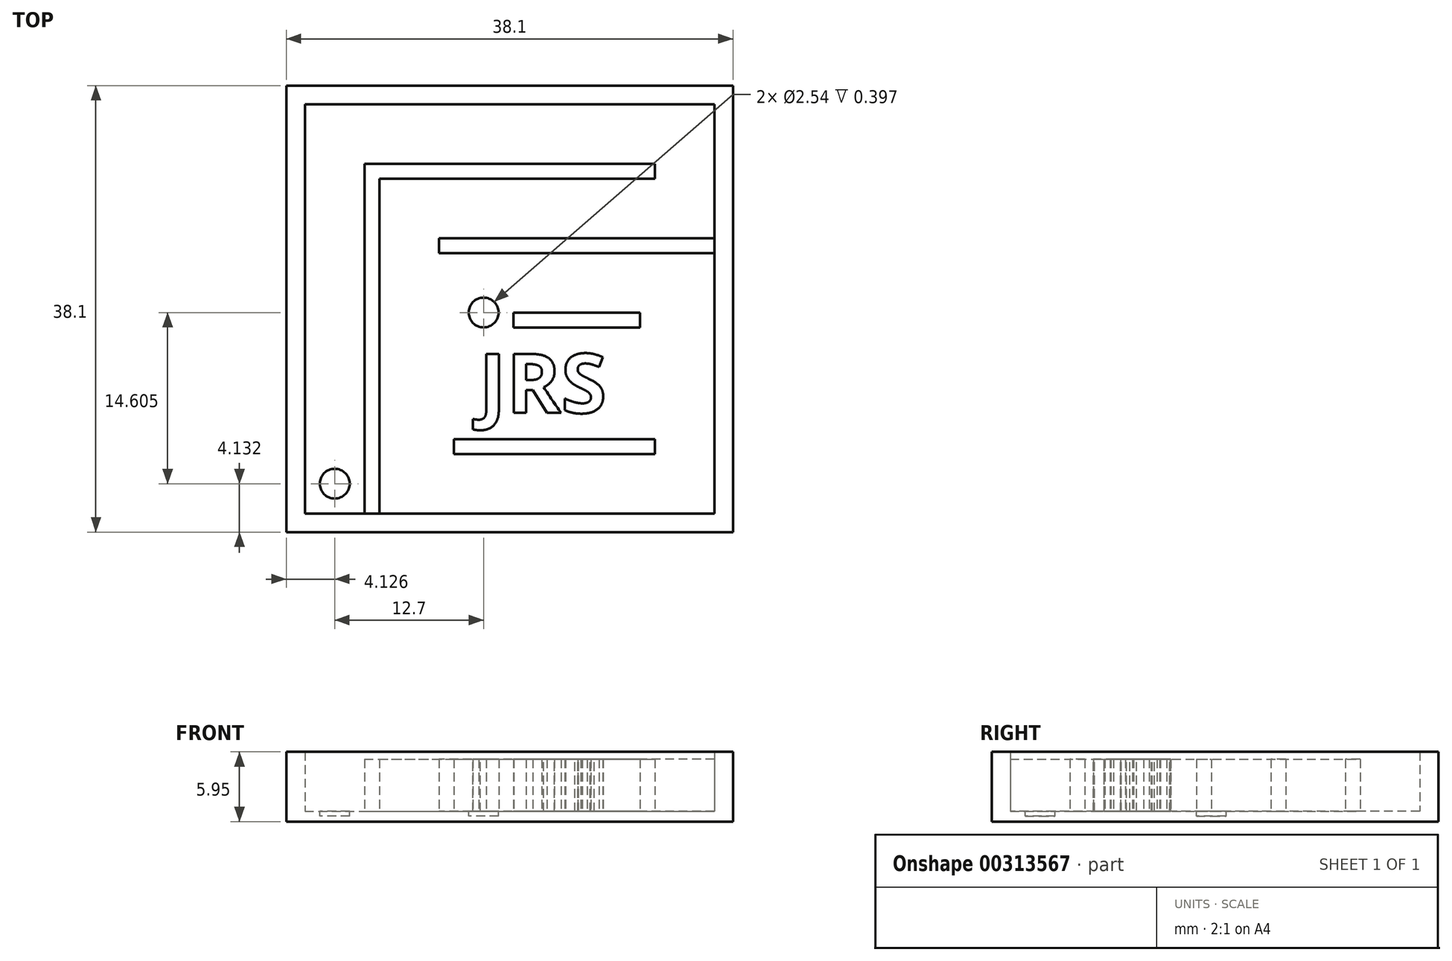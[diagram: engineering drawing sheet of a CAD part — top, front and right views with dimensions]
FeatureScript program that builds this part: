
annotation { "Feature Type Name" : "Feature", "Feature Type Description" : "" }
export const myFeature = defineFeature(function(context is Context, id is Id, definition is map)
    precondition{}
    {
        {
            var Q0;
            Q0=qCreatedBy(makeId("Top.planeOp"),FACE);
            var sketch = newSketch(context, id + "F0", { "sketchPlane" : qUnion([Q0])});
            skLineSegment(sketch, "E0.bottom", {"start": v(-20.77, 18.13) * mm, "end": v(17.33, 18.13) * mm});
            skLineSegment(sketch, "E0.top", {"start": v(-20.77, -19.97) * mm, "end": v(17.33, -19.97) * mm});
            skLineSegment(sketch, "E0.left", {"start": v(-20.77, 18.13) * mm, "end": v(-20.77, -19.97) * mm});
            skLineSegment(sketch, "E0.right", {"start": v(17.33, 18.13) * mm, "end": v(17.33, -19.97) * mm});
            skSolve(sketch);
        }
        {
            var Q0;
            Q0=makeQuery(id+"F0.imprint","IMPRINT",FACE,{"disambiguationData":[TD([[makeQuery(id+"F0.imprint","IMPRINT",EDGE,{"derivedFrom":sQuery(id+"F0.wireOp",EDGE,"E0.bottom")}),-1.0]])]});
            extrude(context, id + "F1", {"entities" : qUnion([Q0]), "depth" : 0.08 * mm});
        }
        {
            var Q0;
            Q0=makeQuery(id+"F1.opExtrude","CAP_FACE",FACE,{"disambiguationData":[OSD([sQuery(id+"F0.wireOp",EDGE,"E0.bottom"),sQuery(id+"F0.wireOp",EDGE,"E0.top"),sQuery(id+"F0.wireOp",EDGE,"E0.left"),sQuery(id+"F0.wireOp",EDGE,"E0.right")])],"isStart":false});
            var sketch = newSketch(context, id + "F2", { "sketchPlane" : qUnion([Q0])});
            skLineSegment(sketch, "E1.0", {"start": v(-19.18, 16.55) * mm, "end": v(15.74, 16.55) * mm});
            skLineSegment(sketch, "E1.1", {"start": v(-19.18, 16.55) * mm, "end": v(-19.18, -18.38) * mm});
            skLineSegment(sketch, "E1.2", {"start": v(-19.18, -18.38) * mm, "end": v(15.74, -18.38) * mm});
            skLineSegment(sketch, "E1.3", {"start": v(15.74, 16.55) * mm, "end": v(15.74, -18.38) * mm});
            skSolve(sketch);
        }
        {
            var Q0;
            Q0=makeQuery(id+"F2.imprint","IMPRINT",FACE,{"disambiguationData":[TD([[makeQuery(id+"F2.imprint","IMPRINT",EDGE,{"derivedFrom":sQuery(id+"F2.wireOp",EDGE,"E1.0")}),1.0]])]});
            extrude(context, id + "F3", {"entities" : qUnion([Q0]), "operationType" : NewBodyOperationType.ADD, "depth" : 5.08 * mm});
        }
        {
            var Q0;
            Q0=makeQuery(id+"F1.opExtrude","CAP_FACE",FACE,{"disambiguationData":[OSD([sQuery(id+"F0.wireOp",EDGE,"E0.bottom"),sQuery(id+"F0.wireOp",EDGE,"E0.top"),sQuery(id+"F0.wireOp",EDGE,"E0.left"),sQuery(id+"F0.wireOp",EDGE,"E0.right")])],"isStart":false});
            var sketch = newSketch(context, id + "F4", { "sketchPlane" : qUnion([Q0])});
            skLineSegment(sketch, "E2.bottom", {"start": v(-14.1, -18.38) * mm, "end": v(-12.83, -18.38) * mm});
            skLineSegment(sketch, "E2.top", {"start": v(-14.1, 11.47) * mm, "end": v(-12.83, 11.47) * mm});
            skLineSegment(sketch, "E2.left", {"start": v(-14.1, -18.38) * mm, "end": v(-14.1, 11.47) * mm});
            skLineSegment(sketch, "E2.right", {"start": v(-12.83, -18.38) * mm, "end": v(-12.83, 11.47) * mm});
            skLineSegment(sketch, "E3.bottom", {"start": v(-12.83, 11.47) * mm, "end": v(10.66, 11.47) * mm});
            skLineSegment(sketch, "E3.top", {"start": v(-12.83, 10.2) * mm, "end": v(10.66, 10.2) * mm});
            skLineSegment(sketch, "E3.left", {"start": v(-12.83, 11.47) * mm, "end": v(-12.83, 10.2) * mm});
            skLineSegment(sketch, "E3.right", {"start": v(10.66, 11.47) * mm, "end": v(10.66, 10.2) * mm});
            skLineSegment(sketch, "E4.bottom", {"start": v(15.74, 3.85) * mm, "end": v(-7.75, 3.85) * mm});
            skLineSegment(sketch, "E4.top", {"start": v(15.74, 5.12) * mm, "end": v(-7.75, 5.12) * mm});
            skLineSegment(sketch, "E4.left", {"start": v(15.74, 3.85) * mm, "end": v(15.74, 5.12) * mm});
            skLineSegment(sketch, "E4.right", {"start": v(-7.75, 3.85) * mm, "end": v(-7.75, 5.12) * mm});
            skLineSegment(sketch, "E5.bottom", {"start": v(-7.75, 3.85) * mm, "end": v(-6.48, 3.85) * mm});
            skLineSegment(sketch, "E5.top", {"start": v(-7.75, -13.3) * mm, "end": v(-6.48, -13.3) * mm});
            skLineSegment(sketch, "E5.left", {"start": v(-7.75, 3.85) * mm, "end": v(-7.75, -13.3) * mm});
            skLineSegment(sketch, "E5.right", {"start": v(-6.48, 3.85) * mm, "end": v(-6.48, -13.3) * mm});
            skLineSegment(sketch, "E6.bottom", {"start": v(-6.48, -13.3) * mm, "end": v(10.66, -13.3) * mm});
            skLineSegment(sketch, "E6.top", {"start": v(-6.48, -12.04) * mm, "end": v(10.66, -12.04) * mm});
            skLineSegment(sketch, "E6.left", {"start": v(-6.48, -13.3) * mm, "end": v(-6.48, -12.04) * mm});
            skLineSegment(sketch, "E6.right", {"start": v(10.66, -13.3) * mm, "end": v(10.66, -12.04) * mm});
            skLineSegment(sketch, "E7.bottom", {"start": v(10.66, -12.04) * mm, "end": v(9.4, -12.04) * mm});
            skLineSegment(sketch, "E7.top", {"start": v(10.66, -1.23) * mm, "end": v(9.4, -1.23) * mm});
            skLineSegment(sketch, "E7.left", {"start": v(10.66, -12.04) * mm, "end": v(10.66, -1.23) * mm});
            skLineSegment(sketch, "E7.right", {"start": v(9.4, -12.04) * mm, "end": v(9.4, -1.23) * mm});
            skLineSegment(sketch, "E8.bottom", {"start": v(9.4, -1.23) * mm, "end": v(-1.4, -1.23) * mm});
            skLineSegment(sketch, "E8.top", {"start": v(9.4, -2.5) * mm, "end": v(-1.4, -2.5) * mm});
            skLineSegment(sketch, "E8.left", {"start": v(9.4, -1.23) * mm, "end": v(9.4, -2.5) * mm});
            skLineSegment(sketch, "E8.right", {"start": v(-1.4, -1.23) * mm, "end": v(-1.4, -2.5) * mm});
            skCircle(sketch, "E9", {"center": v(-3.94, -1.23) * mm, "radius": 1.27 * mm});
            skCircle(sketch, "E10", {"center": v(-16.64, -15.84) * mm, "radius": 1.27 * mm});
            skSolve(sketch);
        }
        {
            var Q0;
            Q0=makeQuery(id+"F4.imprint","IMPRINT",FACE,{"disambiguationData":[TD([[makeQuery(id+"F4.imprint","IMPRINT",EDGE,{"derivedFrom":sQuery(id+"F4.wireOp",EDGE,"E3.bottom")}),-1.0]])]});
            var Q1;
            Q1=makeQuery(id+"F4.imprint","IMPRINT",FACE,{"disambiguationData":[TD([[makeQuery(id+"F4.imprint","IMPRINT",EDGE,{"derivedFrom":sQuery(id+"F4.wireOp",EDGE,"E4.bottom")}),-1.0]])]});
            var Q2;
            Q2=makeQuery(id+"F4.imprint","IMPRINT",FACE,{"disambiguationData":[TD([[makeQuery(id+"F4.imprint","IMPRINT",EDGE,{"derivedFrom":sQuery(id+"F4.wireOp",EDGE,"E5.bottom")}),-1.0]])]});
            var Q3;
            Q3=makeQuery(id+"F4.imprint","IMPRINT",FACE,{"disambiguationData":[TD([[makeQuery(id+"F4.imprint","IMPRINT",EDGE,{"derivedFrom":sQuery(id+"F4.wireOp",EDGE,"E2.bottom")}),1.0]])]});
            var Q4;
            Q4=makeQuery(id+"F4.imprint","IMPRINT",FACE,{"disambiguationData":[TD([[makeQuery(id+"F4.imprint","IMPRINT",EDGE,{"derivedFrom":sQuery(id+"F4.wireOp",EDGE,"E8.bottom")}),1.0]])]});
            var Q5;
            Q5=makeQuery(id+"F4.imprint","IMPRINT",FACE,{"disambiguationData":[TD([[makeQuery(id+"F4.imprint","IMPRINT",EDGE,{"derivedFrom":sQuery(id+"F4.wireOp",EDGE,"LeORAs4u-zZRo-tqkG-Ucmf-BZyhD3jljP38.bottom")}),-1.0]])]});
            var Q6;
            Q6=makeQuery(id+"F4.imprint","IMPRINT",FACE,{"disambiguationData":[TD([[makeQuery(id+"F4.imprint","IMPRINT",EDGE,{"derivedFrom":sQuery(id+"F4.wireOp",EDGE,"E7.bottom")}),-1.0]])]});
            var Q7;
            Q7=makeQuery(id+"F4.imprint","IMPRINT",FACE,{"disambiguationData":[TD([[makeQuery(id+"F4.imprint","IMPRINT",EDGE,{"derivedFrom":sQuery(id+"F4.wireOp",EDGE,"E6.bottom")}),1.0]])]});
            extrude(context, id + "F5", {"entities" : qUnion([Q0, Q1, Q2, Q3, Q4, Q5, Q6, Q7]), "operationType" : NewBodyOperationType.ADD, "depth" : 4.44 * mm});
        }
        {
            var Q0;
            Q0 = qSketchRegion(id + "F0", true);
            extrude(context, id + "F6", {"entities" : qUnion([Q0]), "operationType" : NewBodyOperationType.ADD, "oppositeDirection" : true, "depth" : 0.8 * mm});
        }
        {
            var Q0;
            Q0=makeQuery(id+"F1.opExtrude","CAP_FACE",FACE,{"disambiguationData":[OSD([sQuery(id+"F0.wireOp",EDGE,"E0.bottom"),sQuery(id+"F0.wireOp",EDGE,"E0.top"),sQuery(id+"F0.wireOp",EDGE,"E0.left"),sQuery(id+"F0.wireOp",EDGE,"E0.right")])],"isStart":false});
            var sketch = newSketch(context, id + "F7", { "sketchPlane" : qUnion([Q0])});
            skText(sketch, "E11", { "text": "JRS", "fontName": "OpenSans-Bold.ttf"});
            skPoint(sketch, "E12", {"position": v(1.45, -12.04) * mm});
            const initialGuessF7  = {"E11": [-0.00434, -0.0098, 1, 0, 0.00508]};
            skSetInitialGuess(sketch, initialGuessF7);
            skSolve(sketch);
        }
        {
            var Q0;
            Q0 = qSketchRegion(id + "F7", true);
            extrude(context, id + "F8", {"entities" : qUnion([Q0]), "operationType" : NewBodyOperationType.ADD, "depth" : 4.44 * mm});
        }
        {
            var Q0;
            Q0=makeQuery(id+"F4.imprint","IMPRINT",FACE,{"disambiguationData":[TD([[makeQuery(id+"F4.imprint","IMPRINT",EDGE,{"derivedFrom":sQuery(id+"F4.wireOp",EDGE,"E10")}),1.0]])]});
            var Q1;
            Q1=makeQuery(id+"F4.imprint","IMPRINT",FACE,{"disambiguationData":[TD([[makeQuery(id+"F4.imprint","IMPRINT",EDGE,{"derivedFrom":sQuery(id+"F4.wireOp",EDGE,"E9")}),1.0]])]});
            extrude(context, id + "F9", {"entities" : qUnion([Q0, Q1]), "operationType" : NewBodyOperationType.REMOVE, "oppositeDirection" : true, "depth" : 0.4 * mm});
        }
    });
